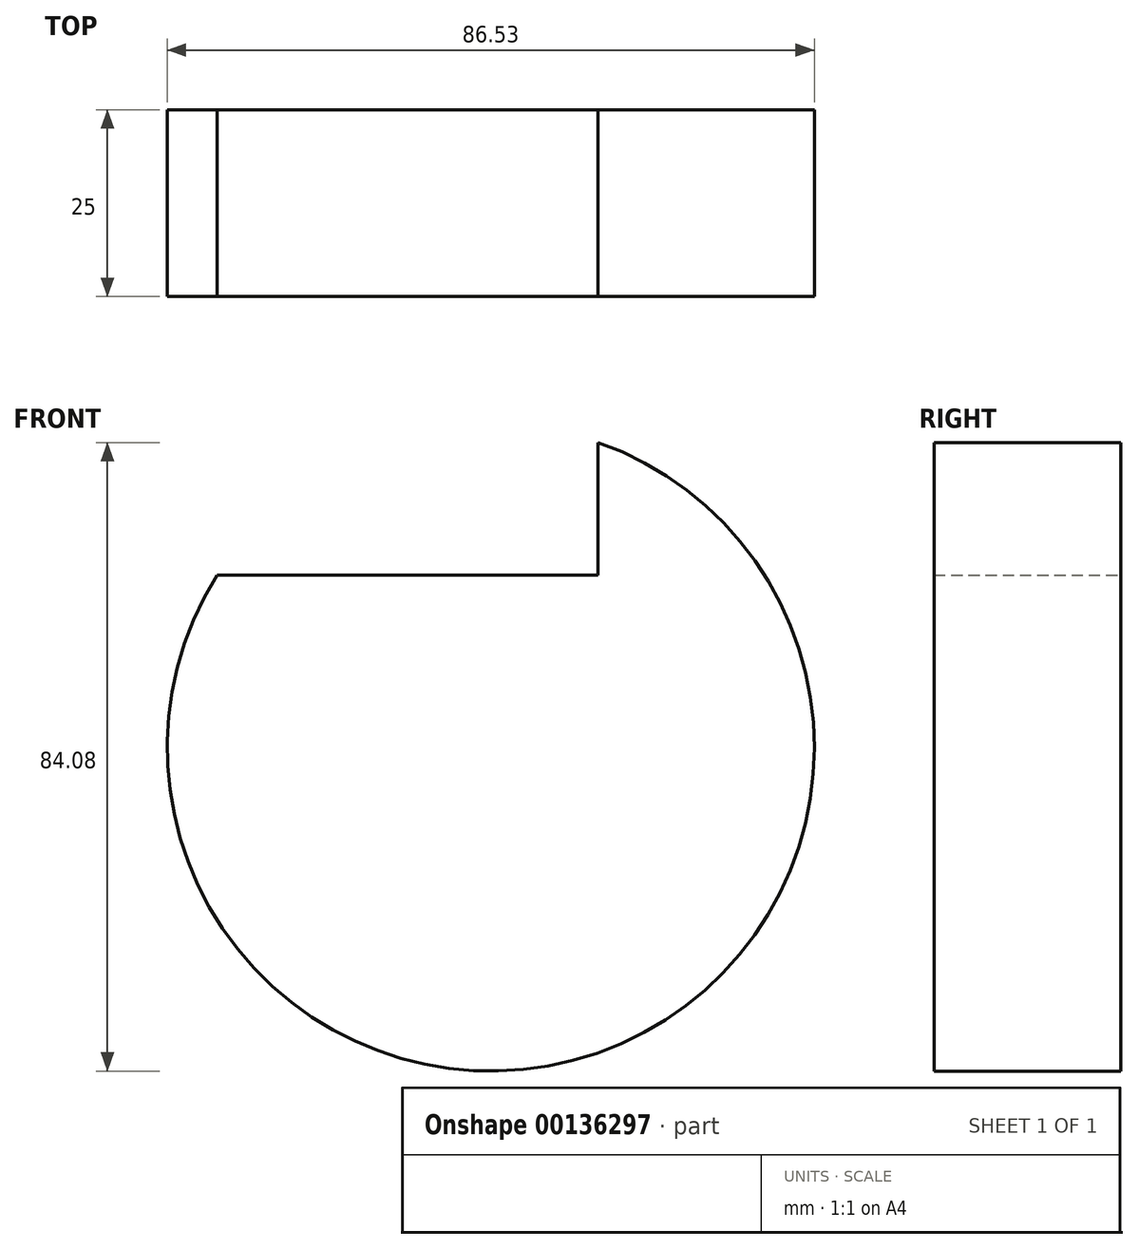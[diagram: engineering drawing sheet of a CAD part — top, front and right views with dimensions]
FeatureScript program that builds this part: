
annotation { "Feature Type Name" : "Feature", "Feature Type Description" : "" }
export const myFeature = defineFeature(function(context is Context, id is Id, definition is map)
    precondition{}
    {
        {
            var Q0;
            Q0=qCreatedBy(makeId("Front.planeOp"),FACE);
            var sketch = newSketch(context, id + "F0", { "sketchPlane" : qUnion([Q0])});
            skLineSegment(sketch, "E0.bottom", {"start": v(-34.8, 31.96) * mm, "end": v(36.97, 31.96) * mm});
            skLineSegment(sketch, "E0.top", {"start": v(-34.8, -33.7) * mm, "end": v(36.97, -33.7) * mm});
            skLineSegment(sketch, "E0.left", {"start": v(-34.8, 31.96) * mm, "end": v(-34.8, -33.7) * mm});
            skLineSegment(sketch, "E0.right", {"start": v(36.97, 31.96) * mm, "end": v(36.97, -33.7) * mm});
            skCircle(sketch, "E1", {"center": v(22.61, -56.75) * mm, "radius": 43.26 * mm});
            skSolve(sketch);
        }
        {
            var Q0;
            {var subQ0=sQuery(id+"F0.wireOp",EDGE,"E0.right");var subQ1=sQuery(id+"F0.wireOp",EDGE,"E0.top");var subQ2=makeQuery(id+"F0.imprint","INTERSECT",VERTEX,{"derivedFrom":[subQ1,subQ0]});Q0=makeQuery(id+"F0.imprint","IMPRINT",FACE,{"disambiguationData":[TD([[makeQuery(id+"F0.imprint","IMPRINT",EDGE,{"disambiguationData":[TD([[subQ2,1.0]])],"derivedFrom":subQ1}),-1.0]])]});}
            extrude(context, id + "F1", {"entities" : qUnion([Q0]), "depth" : 25 * mm});
        }
    });
